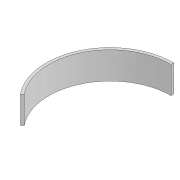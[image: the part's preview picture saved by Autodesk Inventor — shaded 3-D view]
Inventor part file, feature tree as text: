
AUTODESK INVENTOR PART (.ipt)
format: ipt  version: 2022 (Build 260153000, 153)  size: 91,648 bytes
history: native  units: mm
features: extrude x1, sketch x1
ambient origin geometry x8: Origin, YZ Plane, XZ Plane, XY Plane, X Axis, Y Axis, Z Axis, Center Point
bodies: Body1 (feature_tree)
feature tree (2):
  extrude  "Extrusion1"  Depth=45.0mm
  sketch  "Sketch2"  dims[d12=20.0mm d13=0.0mm d14=45.0mm d15=47.0mm d17=2.0mm d18=35.0mm]
